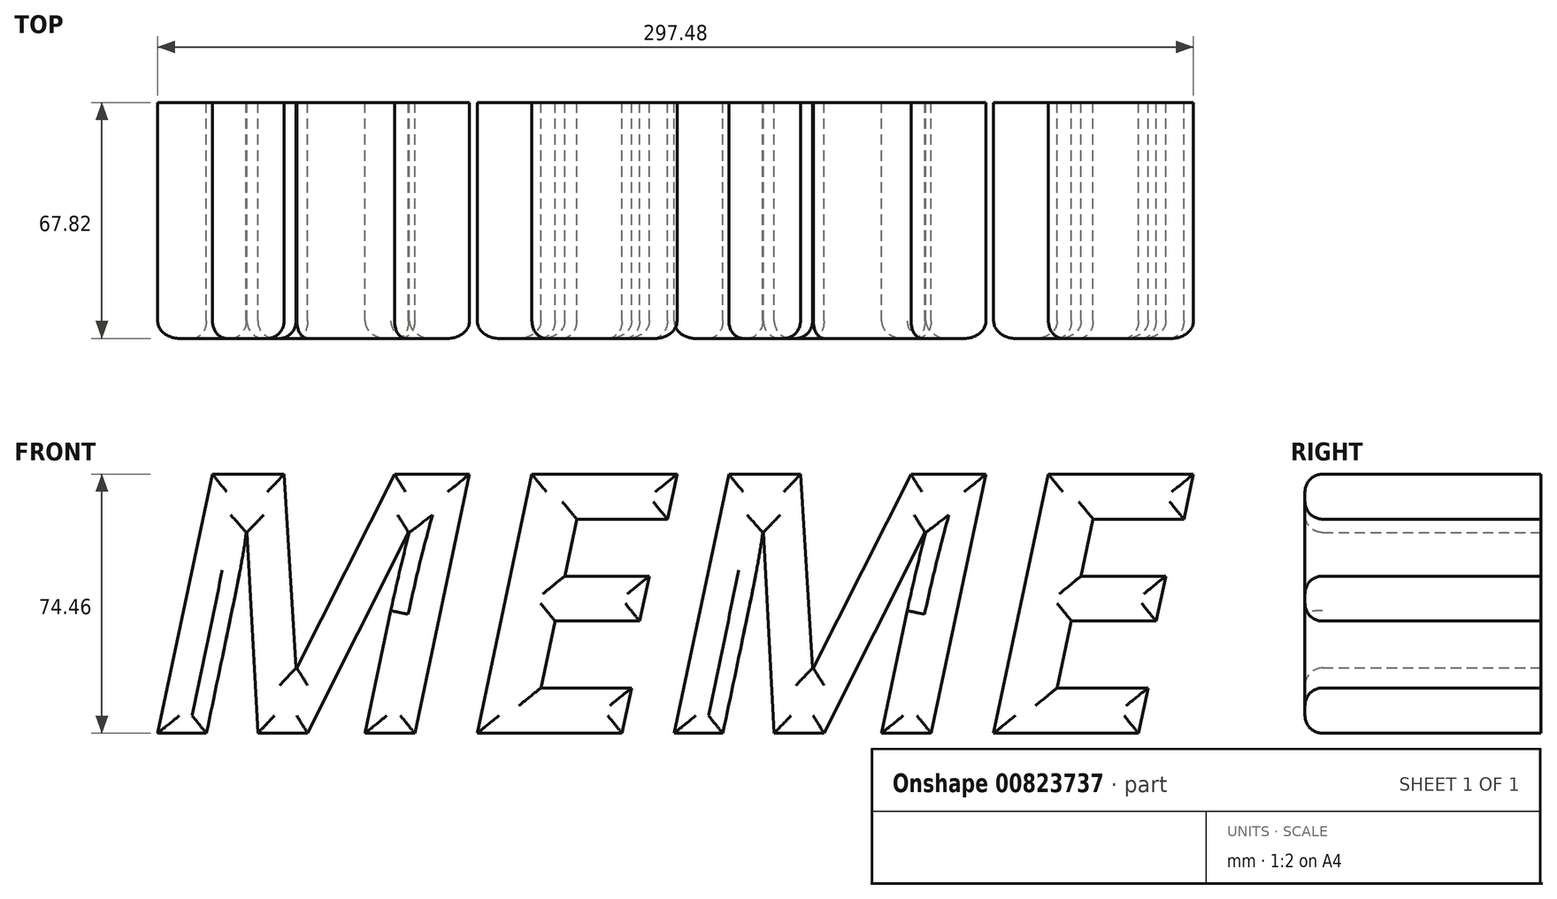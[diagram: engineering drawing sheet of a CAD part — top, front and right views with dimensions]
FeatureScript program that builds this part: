
annotation { "Feature Type Name" : "Feature", "Feature Type Description" : "" }
export const myFeature = defineFeature(function(context is Context, id is Id, definition is map)
    precondition{}
    {
        {
            var Q0;
            Q0=qCreatedBy(makeId("Front.planeOp"),FACE);
            var sketch = newSketch(context, id + "F0", { "sketchPlane" : qUnion([Q0])});
            skText(sketch, "E0", { "text": "MEME", "fontName": "OpenSans-BoldItalic.ttf"});
            const initialGuessF0  = {"E0": [-0.1238, 0.003, 1, 0, 0.0751]};
            skSetInitialGuess(sketch, initialGuessF0);
            skSolve(sketch);
        }
        {
            var Q0;
            Q0 = qSketchRegion(id + "F0", true);
            extrude(context, id + "F1", {"entities" : qUnion([Q0]), "depth" : 67.82 * mm, "offsetDistance" : 25.4 * mm});
        }
        {
            var Q0;
            Q0=makeQuery(id+"F1.opExtrude","CAP_FACE",FACE,{"disambiguationData":[OSD([sQuery(id+"F0.wireOp",EDGE,"E0.sketch_text.stroke-0"),sQuery(id+"F0.wireOp",EDGE,"E0.sketch_text.stroke-1"),sQuery(id+"F0.wireOp",EDGE,"E0.sketch_text.stroke-2"),sQuery(id+"F0.wireOp",EDGE,"E0.sketch_text.stroke-3"),sQuery(id+"F0.wireOp",EDGE,"E0.sketch_text.stroke-4"),sQuery(id+"F0.wireOp",EDGE,"E0.sketch_text.stroke-5"),sQuery(id+"F0.wireOp",EDGE,"E0.sketch_text.stroke-6"),sQuery(id+"F0.wireOp",EDGE,"E0.sketch_text.stroke-7"),sQuery(id+"F0.wireOp",EDGE,"E0.sketch_text.stroke-8"),sQuery(id+"F0.wireOp",EDGE,"E0.sketch_text.stroke-9"),sQuery(id+"F0.wireOp",EDGE,"E0.sketch_text.stroke-10"),sQuery(id+"F0.wireOp",EDGE,"E0.sketch_text.stroke-11"),sQuery(id+"F0.wireOp",EDGE,"E0.sketch_text.stroke-12"),sQuery(id+"F0.wireOp",EDGE,"E0.sketch_text.stroke-13"),sQuery(id+"F0.wireOp",EDGE,"E0.sketch_text.stroke-14"),sQuery(id+"F0.wireOp",EDGE,"E0.sketch_text.stroke-15"),sQuery(id+"F0.wireOp",EDGE,"E0.sketch_text.stroke-16"),sQuery(id+"F0.wireOp",EDGE,"E0.sketch_text.stroke-17")])],"isStart":false});
            var Q1;
            Q1=makeQuery(id+"F1.opExtrude","CAP_FACE",FACE,{"disambiguationData":[OSD([sQuery(id+"F0.wireOp",EDGE,"E0.sketch_text.stroke-18"),sQuery(id+"F0.wireOp",EDGE,"E0.sketch_text.stroke-19"),sQuery(id+"F0.wireOp",EDGE,"E0.sketch_text.stroke-20"),sQuery(id+"F0.wireOp",EDGE,"E0.sketch_text.stroke-21"),sQuery(id+"F0.wireOp",EDGE,"E0.sketch_text.stroke-22"),sQuery(id+"F0.wireOp",EDGE,"E0.sketch_text.stroke-23"),sQuery(id+"F0.wireOp",EDGE,"E0.sketch_text.stroke-24"),sQuery(id+"F0.wireOp",EDGE,"E0.sketch_text.stroke-25"),sQuery(id+"F0.wireOp",EDGE,"E0.sketch_text.stroke-26"),sQuery(id+"F0.wireOp",EDGE,"E0.sketch_text.stroke-27"),sQuery(id+"F0.wireOp",EDGE,"E0.sketch_text.stroke-28"),sQuery(id+"F0.wireOp",EDGE,"E0.sketch_text.stroke-29")])],"isStart":false});
            var Q2;
            Q2=makeQuery(id+"F1.opExtrude","CAP_EDGE",EDGE,{"disambiguationData":[OSD([sQuery(id+"F0.wireOp",EDGE,"E0.sketch_text.stroke-39")])],"isStart":false});
            var Q3;
            Q3=makeQuery(id+"F1.opExtrude","CAP_FACE",FACE,{"disambiguationData":[OSD([sQuery(id+"F0.wireOp",EDGE,"E0.sketch_text.stroke-30"),sQuery(id+"F0.wireOp",EDGE,"E0.sketch_text.stroke-31"),sQuery(id+"F0.wireOp",EDGE,"E0.sketch_text.stroke-32"),sQuery(id+"F0.wireOp",EDGE,"E0.sketch_text.stroke-33"),sQuery(id+"F0.wireOp",EDGE,"E0.sketch_text.stroke-34"),sQuery(id+"F0.wireOp",EDGE,"E0.sketch_text.stroke-35"),sQuery(id+"F0.wireOp",EDGE,"E0.sketch_text.stroke-36"),sQuery(id+"F0.wireOp",EDGE,"E0.sketch_text.stroke-37"),sQuery(id+"F0.wireOp",EDGE,"E0.sketch_text.stroke-38"),sQuery(id+"F0.wireOp",EDGE,"E0.sketch_text.stroke-39"),sQuery(id+"F0.wireOp",EDGE,"E0.sketch_text.stroke-40"),sQuery(id+"F0.wireOp",EDGE,"E0.sketch_text.stroke-41"),sQuery(id+"F0.wireOp",EDGE,"E0.sketch_text.stroke-42"),sQuery(id+"F0.wireOp",EDGE,"E0.sketch_text.stroke-43"),sQuery(id+"F0.wireOp",EDGE,"E0.sketch_text.stroke-44"),sQuery(id+"F0.wireOp",EDGE,"E0.sketch_text.stroke-45"),sQuery(id+"F0.wireOp",EDGE,"E0.sketch_text.stroke-46"),sQuery(id+"F0.wireOp",EDGE,"E0.sketch_text.stroke-47")])],"isStart":false});
            var Q4;
            Q4=makeQuery(id+"F1.opExtrude","CAP_FACE",FACE,{"disambiguationData":[OSD([sQuery(id+"F0.wireOp",EDGE,"E0.sketch_text.stroke-48"),sQuery(id+"F0.wireOp",EDGE,"E0.sketch_text.stroke-49"),sQuery(id+"F0.wireOp",EDGE,"E0.sketch_text.stroke-50"),sQuery(id+"F0.wireOp",EDGE,"E0.sketch_text.stroke-51"),sQuery(id+"F0.wireOp",EDGE,"E0.sketch_text.stroke-52"),sQuery(id+"F0.wireOp",EDGE,"E0.sketch_text.stroke-53"),sQuery(id+"F0.wireOp",EDGE,"E0.sketch_text.stroke-54"),sQuery(id+"F0.wireOp",EDGE,"E0.sketch_text.stroke-55"),sQuery(id+"F0.wireOp",EDGE,"E0.sketch_text.stroke-56"),sQuery(id+"F0.wireOp",EDGE,"E0.sketch_text.stroke-57"),sQuery(id+"F0.wireOp",EDGE,"E0.sketch_text.stroke-58"),sQuery(id+"F0.wireOp",EDGE,"E0.sketch_text.stroke-59")])],"isStart":false});
            fillet(context, id + "F2", {"entities" : qUnion([Q0, Q1, Q2, Q3, Q4]), "radius" : 5.08 * mm, "tangentPropagation" : true, "allowEdgeOverflow" : false});
        }
    });
